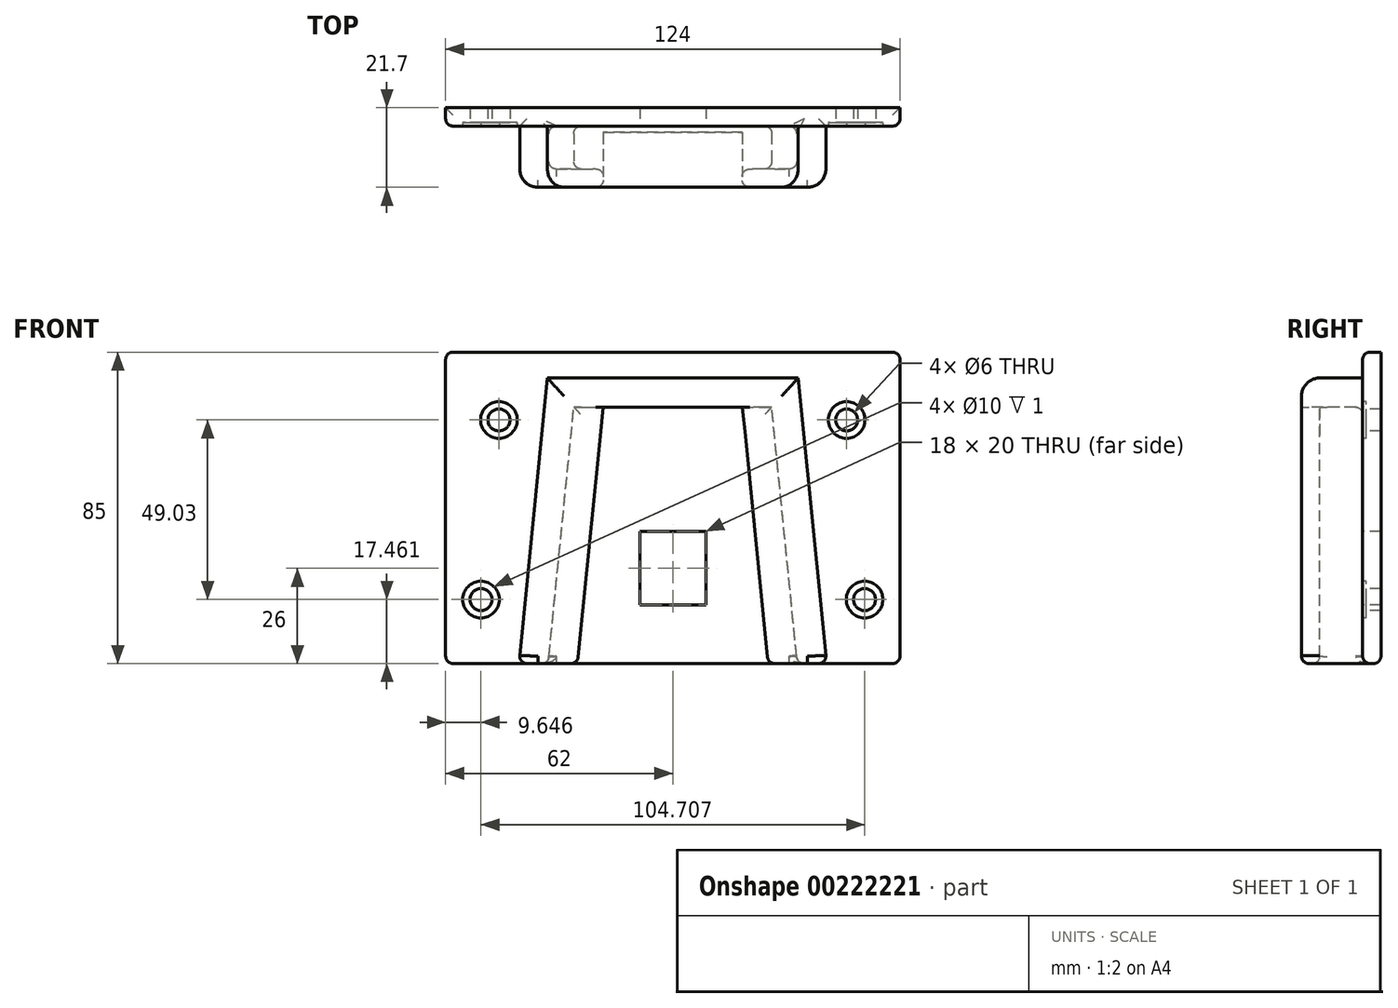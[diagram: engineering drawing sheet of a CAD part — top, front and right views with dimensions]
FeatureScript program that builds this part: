
annotation { "Feature Type Name" : "Feature", "Feature Type Description" : "" }
export const myFeature = defineFeature(function(context is Context, id is Id, definition is map)
    precondition{}
    {
        {
            var Q0;
            Q0=qCreatedBy(makeId("Front.planeOp"),FACE);
            var sketch = newSketch(context, id + "F0", { "sketchPlane" : qUnion([Q0])});
            skLineSegment(sketch, "E0.left", {"start": v(0, 0) * mm, "end": v(0, 0) * mm});
            skLineSegment(sketch, "E1", {"start": v(0, 0) * mm, "end": v(-62, 0) * mm});
            skLineSegment(sketch, "E2", {"start": v(-62, 0) * mm, "end": v(-62, 85) * mm});
            skLineSegment(sketch, "E3", {"start": v(-62, 85) * mm, "end": v(0, 85) * mm});
            skLineSegment(sketch, "E4", {"start": v(0, 102.01) * mm, "end": v(0, -45.63) * mm, "construction": true});
            skLineSegment(sketch, "E5", {"start": v(-34, 0) * mm, "end": v(-27, 70) * mm});
            skLineSegment(sketch, "E6", {"start": v(-27, 70) * mm, "end": v(0, 70) * mm});
            skLineSegment(sketch, "E7", {"start": v(0, 70) * mm, "end": v(2, 70) * mm});
            skPoint(sketch, "E8", {"position": v(-52.35, 17.46) * mm});
            skPoint(sketch, "E9", {"position": v(-47.45, 66.5) * mm});
            skSolve(sketch);
        }
        {
            var Q0;
            Q0=qCreatedBy(makeId("Top.planeOp"),FACE);
            var sketch = newSketch(context, id + "F1", { "sketchPlane" : qUnion([Q0])});
            skLineSegment(sketch, "E10", {"start": v(-34, 0) * mm, "end": v(-34, -11.7) * mm});
            skLineSegment(sketch, "E11", {"start": v(-34, -11.7) * mm, "end": v(-26, -11.7) * mm});
            skLineSegment(sketch, "E12", {"start": v(-26, -11.7) * mm, "end": v(-26, -16.7) * mm});
            skLineSegment(sketch, "E13", {"start": v(-26, -16.7) * mm, "end": v(-42, -16.7) * mm});
            skLineSegment(sketch, "E14", {"start": v(-42, -16.7) * mm, "end": v(-42, 0) * mm});
            skLineSegment(sketch, "E15", {"start": v(-42, 0) * mm, "end": v(-34, 0) * mm});
            skSolve(sketch);
        }
        {
            var Q0;
            Q0=makeQuery(id+"F1.imprint","IMPRINT",FACE,{"disambiguationData":[TD([[makeQuery(id+"F1.imprint","IMPRINT",EDGE,{"derivedFrom":sQuery(id+"F1.wireOp",EDGE,"E10")}),-1.0]])]});
            var Q1;
            Q1=sQuery(id+"F0.wireOp",EDGE,"E5");
            var Q2;
            Q2=sQuery(id+"F0.wireOp",EDGE,"E6");
            var Q3;
            Q3=sQuery(id+"F0.wireOp",EDGE,"E7");
            sweep(context, id + "F2", {"profiles" : qUnion([Q0]), "path" : qUnion([Q1, Q2, Q3])});
        }
        {
            var Q0;
            Q0=qCreatedBy(makeId("Front.planeOp"),FACE);
            var sketch = newSketch(context, id + "F3", { "sketchPlane" : qUnion([Q0])});
            skLineSegment(sketch, "E16.bottom", {"start": v(0, 85) * mm, "end": v(-62, 85) * mm});
            skLineSegment(sketch, "E16.top", {"start": v(0, 0) * mm, "end": v(-62, 0) * mm});
            skLineSegment(sketch, "E16.left", {"start": v(0, 85) * mm, "end": v(0, 0) * mm});
            skLineSegment(sketch, "E16.right", {"start": v(-62, 85) * mm, "end": v(-62, 0) * mm});
            skSolve(sketch);
        }
        {
            var Q0;
            Q0 = qSketchRegion(id + "F3", true);
            var Q1;
            {var subQ3=sQuery(id+"F0.wireOp",EDGE,"E2");Q1=makeQuery(id+"F0.imprint","IMPRINT",FACE,{"disambiguationData":[TD([[makeQuery(id+"F0.imprint","IMPRINT",EDGE,{"derivedFrom":subQ3}),-1.0]])]});}
            extrude(context, id + "F4", {"entities" : qUnion([Q0, Q1]), "operationType" : NewBodyOperationType.ADD, "oppositeDirection" : true, "depth" : 5 * mm});
        }
        {
            var Q0;
            Q0=makeQuery(id+"F2.opSweep","SWEPT_EDGE",EDGE,{"disambiguationData":[OSD([sQuery(id+"F0.wireOp",EDGE,"E5"),sQuery(id+"F1.wireOp",EDGE,"E13"),sQuery(id+"F1.wireOp",EDGE,"E14")])]});
            var Q1;
            Q1=makeQuery(id+"F2.opSweep","SWEPT_EDGE",EDGE,{"disambiguationData":[OSD([sQuery(id+"F0.wireOp",EDGE,"E6"),sQuery(id+"F1.wireOp",EDGE,"E13"),sQuery(id+"F1.wireOp",EDGE,"E14")])]});
            var Q2;
            {var subQ0=sQuery(id+"F1.wireOp",EDGE,"E14");Q2=makeQuery(id+"F4.boolean.opBoolean","SPLIT",EDGE,{"disambiguationData":[topologyDisambiguationEdgeConnected([makeQuery(id+"F4.opExtrude","CAP_FACE",FACE,{"disambiguationData":[OSD([sQuery(id+"F3.wireOp",EDGE,"E16.bottom"),sQuery(id+"F3.wireOp",EDGE,"E16.top"),sQuery(id+"F3.wireOp",EDGE,"E16.left"),sQuery(id+"F3.wireOp",EDGE,"E16.right")])],"isStart":true})])],"derivedFrom":makeQuery(id+"F2.opSweep","SWEPT_EDGE",EDGE,{"disambiguationData":[OSD([sQuery(id+"F0.wireOp",EDGE,"E6"),subQ0,sQuery(id+"F1.wireOp",EDGE,"E15")])]})});}
            var Q3;
            Q3=makeQuery(id+"F2.opSweep","SWEPT_EDGE",EDGE,{"disambiguationData":[OSD([sQuery(id+"F0.wireOp",EDGE,"E5"),sQuery(id+"F1.wireOp",EDGE,"E14"),sQuery(id+"F1.wireOp",EDGE,"E15")])]});
            fillet(context, id + "F5", {"entities" : qUnion([Q0, Q1, Q2, Q3]), "radius" : 5 * mm, "tangentPropagation" : true, "allowEdgeOverflow" : false});
        }
        {
            var Q0;
            Q0=sQuery(id+"F0.wireOp",VERTEX,"E9");
            var Q1;
            Q1=sQuery(id+"F0.wireOp",VERTEX,"E8");
            var Q2;
            Q2=makeQuery(id+"F2.opSweep","SWEPT_BODY",BODY,{"disambiguationData":[OSD([sQuery(id+"F0.wireOp",EDGE,"E7"),sQuery(id+"F1.wireOp",EDGE,"E10"),sQuery(id+"F1.wireOp",EDGE,"E11"),sQuery(id+"F1.wireOp",EDGE,"E12"),sQuery(id+"F1.wireOp",EDGE,"E13"),sQuery(id+"F1.wireOp",EDGE,"E14"),sQuery(id+"F1.wireOp",EDGE,"E15")])]});
            hole(context, id + "F6", {"style" : HoleStyle.C_BORE, "endStyle" : HoleEndStyle.THROUGH, "holeDiameter" : 6 * mm, "cBoreDiameter" : 10 * mm, "cBoreDepth" : 1 * mm, "locations" : qUnion([Q0, Q1]), "scope" : qUnion([Q2]), "isTappedThrough" : true});
        }
        {
            var Q0;
            Q0=qCreatedBy(makeId("Front.planeOp"),FACE);
            var sketch = newSketch(context, id + "F7", { "sketchPlane" : qUnion([Q0])});
            skLineSegment(sketch, "E17.bottom", {"start": v(0, 36) * mm, "end": v(-9, 36) * mm});
            skLineSegment(sketch, "E17.top", {"start": v(0, 16) * mm, "end": v(-9, 16) * mm});
            skLineSegment(sketch, "E17.left", {"start": v(0, 36) * mm, "end": v(0, 16) * mm});
            skLineSegment(sketch, "E17.right", {"start": v(-9, 36) * mm, "end": v(-9, 16) * mm});
            skSolve(sketch);
        }
        {
            var Q0;
            Q0=makeQuery(id+"F7.imprint","IMPRINT",FACE,{"disambiguationData":[TD([[makeQuery(id+"F7.imprint","IMPRINT",EDGE,{"derivedFrom":sQuery(id+"F7.wireOp",EDGE,"E17.bottom")}),1.0]])]});
            extrude(context, id + "F8", {"entities" : qUnion([Q0]), "operationType" : NewBodyOperationType.REMOVE, "oppositeDirection" : true, "depth" : 6 * mm});
        }
        {
            var Q0;
            {var subQ0=makeQuery(id+"F2.opSweep","SWEPT_FACE",FACE,{"disambiguationData":[OSD([sQuery(id+"F0.wireOp",EDGE,"E5"),sQuery(id+"F1.wireOp",EDGE,"E13")])]});Q0=makeQuery(id+"F11.boolean.opBoolean","MERGE",FACE,{"derivedFrom":[subQ0,makeQuery(id+"F11.opPattern","COPY",FACE,{"derivedFrom":subQ0,"instanceName":"1"})]});}
            var sketch = newSketch(context, id + "F9", { "sketchPlane" : qUnion([Q0])});
            skLineSegment(sketch, "E18", {"start": v(-19.8, 62.04) * mm, "end": v(-18.98, 70.03) * mm});
            skLineSegment(sketch, "E19", {"start": v(-18.98, 70.03) * mm, "end": v(2, 70.03) * mm});
            skLineSegment(sketch, "E20", {"start": v(-19.8, 62.04) * mm, "end": v(2.8, 62.04) * mm});
            skSolve(sketch);
        }
        {
            var Q0;
            Q0=makeQuery(id+"F9.imprint","IMPRINT",FACE,{"disambiguationData":[TD([[makeQuery(id+"F9.imprint","IMPRINT",EDGE,{"derivedFrom":sQuery(id+"F9.wireOp",EDGE,"E18")}),-1.0]])]});
            extrude(context, id + "F10", {"entities" : qUnion([Q0]), "operationType" : NewBodyOperationType.REMOVE, "oppositeDirection" : true, "depth" : 15 * mm});
        }
        {
            var Q0;
            Q0=makeQuery(id+"F2.opSweep","SWEPT_BODY",BODY,{"disambiguationData":[OSD([sQuery(id+"F0.wireOp",EDGE,"E7"),sQuery(id+"F1.wireOp",EDGE,"E10"),sQuery(id+"F1.wireOp",EDGE,"E11"),sQuery(id+"F1.wireOp",EDGE,"E12"),sQuery(id+"F1.wireOp",EDGE,"E13"),sQuery(id+"F1.wireOp",EDGE,"E14"),sQuery(id+"F1.wireOp",EDGE,"E15")])]});
            var Q1;
            Q1=qCreatedBy(makeId("Right.planeOp"),FACE);
            mirror(context, id + "F11", {"operationType" : NewBodyOperationType.ADD, "entities" : qUnion([Q0]), "mirrorPlane" : qUnion([Q1])});
        }
        {
            var Q0;
            Q0=makeQuery(id+"F2.opSweep","SWEPT_EDGE",EDGE,{"disambiguationData":[OSD([sQuery(id+"F0.wireOp",EDGE,"E5"),sQuery(id+"F1.wireOp",EDGE,"E10"),sQuery(id+"F1.wireOp",EDGE,"E11")])]});
            var Q1;
            {var subQ0=makeQuery(id+"F4.boolean.opBoolean","MERGE",FACE,{"derivedFrom":[makeQuery(id+"F2.opSweep","CAP_FACE",FACE,{"disambiguationData":[OSD([sQuery(id+"F0.wireOp",VERTEX,"E5.start"),sQuery(id+"F1.wireOp",EDGE,"E10"),sQuery(id+"F1.wireOp",EDGE,"E11"),sQuery(id+"F1.wireOp",EDGE,"E12"),sQuery(id+"F1.wireOp",EDGE,"E13"),sQuery(id+"F1.wireOp",EDGE,"E14"),sQuery(id+"F1.wireOp",EDGE,"E15")])],"isStart":true}),makeQuery(id+"F4.opExtrude","SWEPT_FACE",FACE,{"disambiguationData":[OSD([sQuery(id+"F3.wireOp",EDGE,"E16.top")])]})]});Q1=makeQuery(id+"F11.boolean.opBoolean","MERGE",FACE,{"derivedFrom":[subQ0,makeQuery(id+"F11.opPattern","COPY",FACE,{"derivedFrom":subQ0,"instanceName":"1"})]});}
            var Q2;
            Q2=makeQuery(id+"F11.opPattern","COPY",EDGE,{"derivedFrom":makeQuery(id+"F2.opSweep","SWEPT_EDGE",EDGE,{"disambiguationData":[OSD([sQuery(id+"F0.wireOp",EDGE,"E5"),sQuery(id+"F1.wireOp",EDGE,"E10"),sQuery(id+"F1.wireOp",EDGE,"E11")])]}),"instanceName":"1"});
            var Q3;
            Q3=makeQuery(id+"F2.opSweep","SWEPT_EDGE",EDGE,{"disambiguationData":[OSD([sQuery(id+"F0.wireOp",EDGE,"E5"),sQuery(id+"F1.wireOp",EDGE,"E12"),sQuery(id+"F1.wireOp",EDGE,"E13")])]});
            var Q4;
            {var subQ0=makeQuery(id+"F2.opSweep","SWEPT_EDGE",EDGE,{"disambiguationData":[OSD([sQuery(id+"F0.wireOp",EDGE,"E6"),sQuery(id+"F1.wireOp",EDGE,"E12"),sQuery(id+"F1.wireOp",EDGE,"E13")])]});Q4=makeQuery(id+"F11.boolean.opBoolean","MERGE",EDGE,{"derivedFrom":[subQ0,makeQuery(id+"F11.opPattern","COPY",EDGE,{"derivedFrom":subQ0,"instanceName":"1"})]});}
            var Q5;
            Q5=makeQuery(id+"F11.opPattern","COPY",EDGE,{"derivedFrom":makeQuery(id+"F2.opSweep","SWEPT_EDGE",EDGE,{"disambiguationData":[OSD([sQuery(id+"F0.wireOp",EDGE,"E5"),sQuery(id+"F1.wireOp",EDGE,"E12"),sQuery(id+"F1.wireOp",EDGE,"E13")])]}),"instanceName":"1"});
            var Q6;
            Q6=makeQuery(id+"F2.opSweep","SWEPT_EDGE",EDGE,{"disambiguationData":[OSD([sQuery(id+"F0.wireOp",EDGE,"E5"),sQuery(id+"F1.wireOp",EDGE,"E11"),sQuery(id+"F1.wireOp",EDGE,"E12")])]});
            var Q7;
            {var subQ0=makeQuery(id+"F2.opSweep","SWEPT_EDGE",EDGE,{"disambiguationData":[OSD([sQuery(id+"F0.wireOp",EDGE,"E6"),sQuery(id+"F1.wireOp",EDGE,"E11"),sQuery(id+"F1.wireOp",EDGE,"E12")])]});Q7=makeQuery(id+"F11.boolean.opBoolean","MERGE",EDGE,{"derivedFrom":[subQ0,makeQuery(id+"F11.opPattern","COPY",EDGE,{"derivedFrom":subQ0,"instanceName":"1"})]});}
            var Q8;
            Q8=makeQuery(id+"F11.opPattern","COPY",EDGE,{"derivedFrom":makeQuery(id+"F2.opSweep","SWEPT_EDGE",EDGE,{"disambiguationData":[OSD([sQuery(id+"F0.wireOp",EDGE,"E5"),sQuery(id+"F1.wireOp",EDGE,"E11"),sQuery(id+"F1.wireOp",EDGE,"E12")])]}),"instanceName":"1"});
            var Q9;
            Q9=makeQuery(id+"F4.opExtrude","SWEPT_EDGE",EDGE,{"disambiguationData":[OSD([sQuery(id+"F3.wireOp",EDGE,"E16.bottom"),sQuery(id+"F3.wireOp",EDGE,"E16.right")])]});
            var Q10;
            Q10=makeQuery(id+"F11.opPattern","COPY",EDGE,{"derivedFrom":makeQuery(id+"F4.opExtrude","SWEPT_EDGE",EDGE,{"disambiguationData":[OSD([sQuery(id+"F3.wireOp",EDGE,"E16.bottom"),sQuery(id+"F3.wireOp",EDGE,"E16.right")])]}),"instanceName":"1"});
            fillet(context, id + "F12", {"entities" : qUnion([Q0, Q1, Q2, Q3, Q4, Q5, Q6, Q7, Q8, Q9, Q10]), "radius" : 2 * mm, "tangentPropagation" : true, "allowEdgeOverflow" : false});
        }
        {
            var Q0;
            Q0=makeQuery(id+"F4.opExtrude","CAP_EDGE",EDGE,{"disambiguationData":[OSD([sQuery(id+"F3.wireOp",EDGE,"E16.right")])],"isStart":true});
            var Q1;
            {var subQ0=makeQuery(id+"F10.boolean.opBoolean","COPY",EDGE,{"derivedFrom":makeQuery(id+"F10.opExtrude","CAP_EDGE",EDGE,{"disambiguationData":[OSD([sQuery(id+"F9.wireOp",EDGE,"E19")])],"isStart":true})});Q1=makeQuery(id+"F11.boolean.opBoolean","MERGE",EDGE,{"derivedFrom":[subQ0,makeQuery(id+"F11.opPattern","COPY",EDGE,{"derivedFrom":subQ0,"instanceName":"1"})]});}
            var Q2;
            Q2=makeQuery(id+"F2.opSweep","SWEPT_EDGE",EDGE,{"disambiguationData":[OSD([sQuery(id+"F0.wireOp",EDGE,"E5"),sQuery(id+"F1.wireOp",EDGE,"E10"),sQuery(id+"F1.wireOp",EDGE,"E15")])]});
            var Q3;
            {var subQ0=sQuery(id+"F1.wireOp",EDGE,"E10");var subQ2=sQuery(id+"F1.wireOp",EDGE,"E15");var subQ3=makeQuery(id+"F2.opSweep","SWEPT_EDGE",EDGE,{"disambiguationData":[OSD([sQuery(id+"F0.wireOp",EDGE,"E6"),subQ0,subQ2])]});var subQ4=makeQuery(id+"F4.boolean.opBoolean","SPLIT",EDGE,{"disambiguationData":[topologyDisambiguationEdgeConnected([makeQuery(id+"F4.opExtrude","CAP_FACE",FACE,{"disambiguationData":[OSD([sQuery(id+"F3.wireOp",EDGE,"E16.bottom"),sQuery(id+"F3.wireOp",EDGE,"E16.top"),sQuery(id+"F3.wireOp",EDGE,"E16.left"),sQuery(id+"F3.wireOp",EDGE,"E16.right")])],"isStart":true})])],"derivedFrom":subQ3});Q3=makeQuery(id+"F11.boolean.opBoolean","MERGE",EDGE,{"derivedFrom":[makeQuery(id+"F4.boolean.opBoolean","SPLIT",EDGE,{"disambiguationData":[topologyDisambiguationEdgeConnected([makeQuery(id+"F2.opSweep","SWEPT_FACE",FACE,{"disambiguationData":[OSD([sQuery(id+"F0.wireOp",EDGE,"E5"),subQ2])]})])],"derivedFrom":subQ3}),subQ4,makeQuery(id+"F11.opPattern","COPY",EDGE,{"derivedFrom":subQ4,"instanceName":"1"})]});}
            var Q4;
            Q4=makeQuery(id+"F11.opPattern","COPY",EDGE,{"derivedFrom":makeQuery(id+"F2.opSweep","SWEPT_EDGE",EDGE,{"disambiguationData":[OSD([sQuery(id+"F0.wireOp",EDGE,"E5"),sQuery(id+"F1.wireOp",EDGE,"E10"),sQuery(id+"F1.wireOp",EDGE,"E15")])]}),"instanceName":"1"});
            fillet(context, id + "F13", {"entities" : qUnion([Q0, Q1, Q2, Q3, Q4]), "radius" : 2 * mm, "tangentPropagation" : true, "allowEdgeOverflow" : false});
        }
    });
